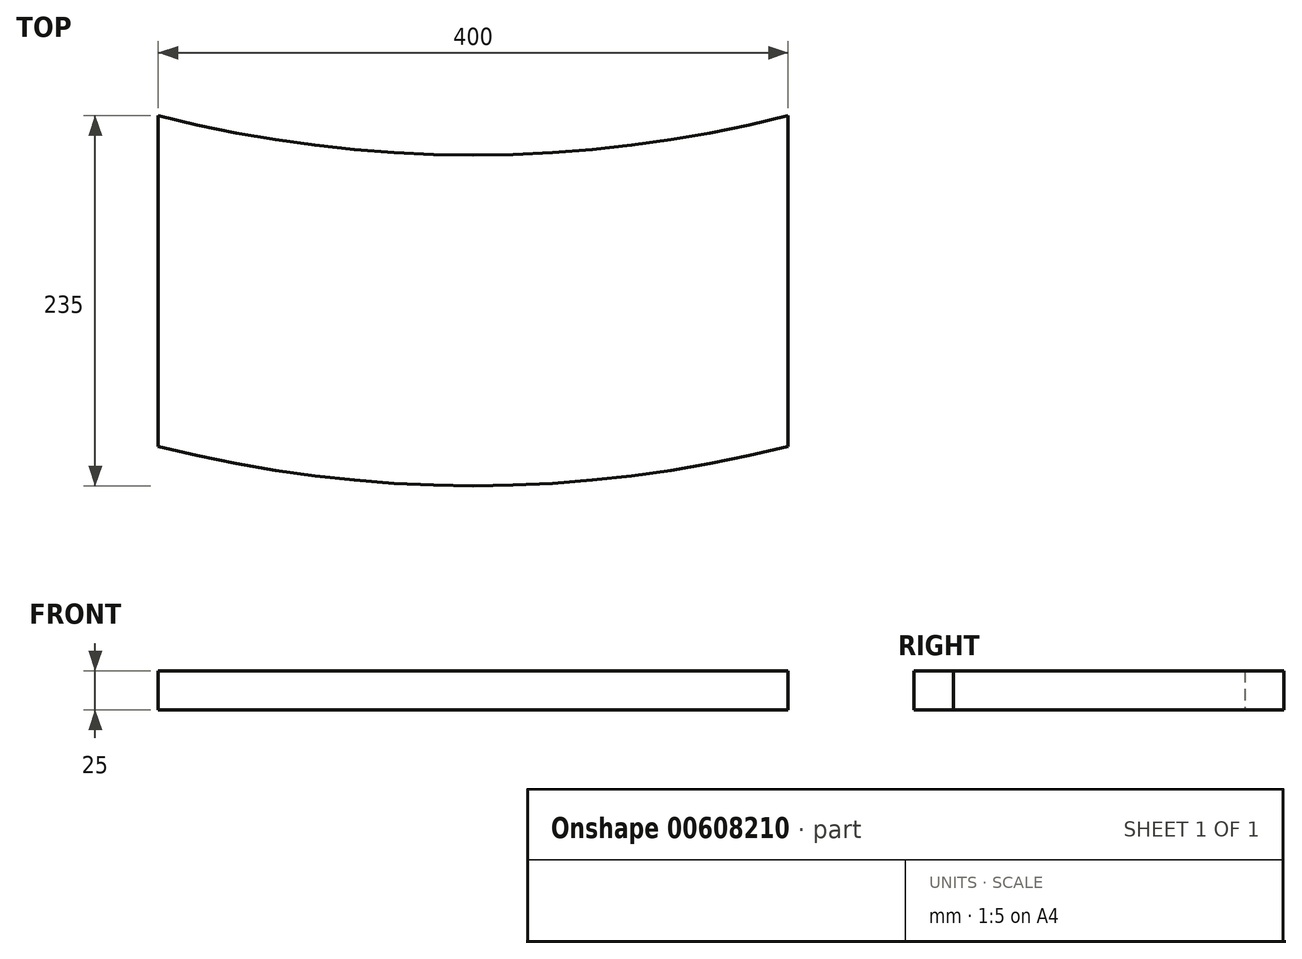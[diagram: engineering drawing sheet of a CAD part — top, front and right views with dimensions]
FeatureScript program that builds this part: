
annotation { "Feature Type Name" : "Feature", "Feature Type Description" : "" }
export const myFeature = defineFeature(function(context is Context, id is Id, definition is map)
    precondition{}
    {
        {
            var Q0;
            Q0=qCreatedBy(makeId("Top.planeOp"),FACE);
            var sketch = newSketch(context, id + "F0", { "sketchPlane" : qUnion([Q0])});
            skLineSegment(sketch, "E0", {"start": v(0, 0) * mm, "end": v(0, -210) * mm});
            skLineSegment(sketch, "E1", {"start": v(400, -210) * mm, "end": v(400, 0) * mm});
            skArc(sketch, "E2", {"start": v(0, 0) * mm, "mid": v(200, -25) * mm, "end": v(400, 0) * mm});
            skArc(sketch, "E3", {"start": v(0, -210) * mm, "mid": v(200, -235) * mm, "end": v(400, -210) * mm});
            skPoint(sketch, "E4.start.orphan", {"position": v(0, -105) * mm});
            skPoint(sketch, "E5.start.orphan", {"position": v(200, -210) * mm});
            skSolve(sketch);
        }
        {
            var Q0;
            Q0 = qSketchRegion(id + "F0", true);
            extrude(context, id + "F1", {"entities" : qUnion([Q0]), "depth" : 25 * mm, "offsetDistance" : 25 * mm});
        }
    });
